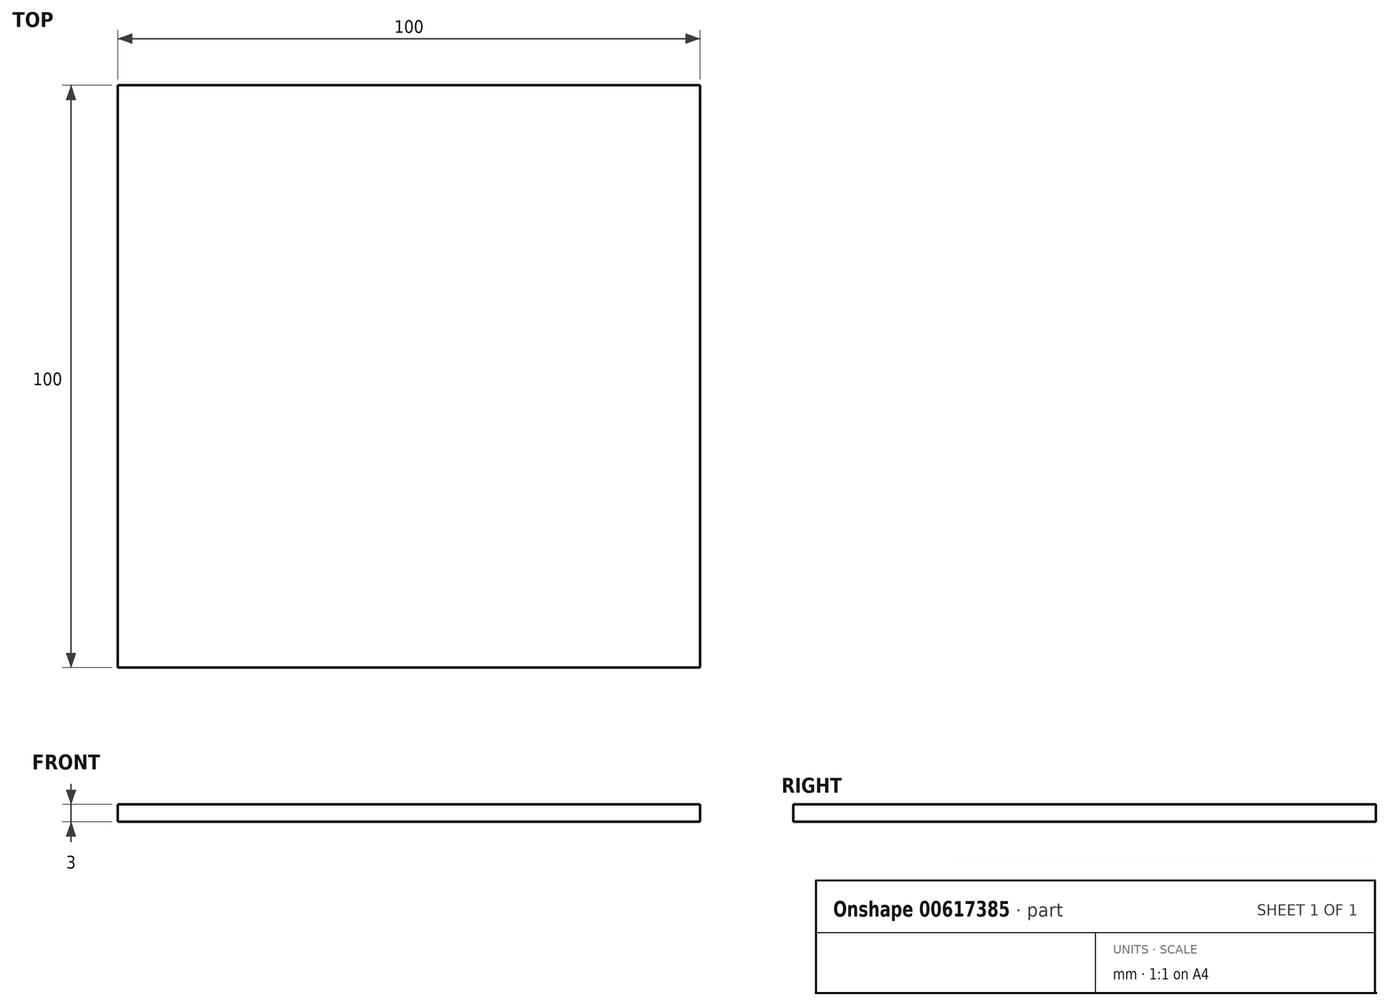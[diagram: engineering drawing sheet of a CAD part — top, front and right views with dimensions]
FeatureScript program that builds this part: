
annotation { "Feature Type Name" : "Feature", "Feature Type Description" : "" }
export const myFeature = defineFeature(function(context is Context, id is Id, definition is map)
    precondition{}
    {
        {
            var Q0;
            Q0=qCreatedBy(makeId("Top.planeOp"),FACE);
            var sketch = newSketch(context, id + "F0", { "sketchPlane" : qUnion([Q0])});
            skLineSegment(sketch, "E0.bottom", {"start": v(50, 50) * mm, "end": v(-50, 50) * mm});
            skLineSegment(sketch, "E0.top", {"start": v(50, -50) * mm, "end": v(-50, -50) * mm});
            skLineSegment(sketch, "E0.left", {"start": v(50, 50) * mm, "end": v(50, -50) * mm});
            skLineSegment(sketch, "E0.right", {"start": v(-50, 50) * mm, "end": v(-50, -50) * mm});
            skPoint(sketch, "E0.middle", {"position": v(0, 0) * mm});
            skSolve(sketch);
        }
        {
            var Q0;
            Q0=makeQuery(id+"F0.imprint","IMPRINT",FACE,{"disambiguationData":[TD([[makeQuery(id+"F0.imprint","IMPRINT",EDGE,{"derivedFrom":sQuery(id+"F0.wireOp",EDGE,"E0.bottom")}),1.0]])]});
            extrude(context, id + "F1", {"entities" : qUnion([Q0]), "depth" : 3 * mm, "offsetDistance" : 25 * mm});
        }
    });
